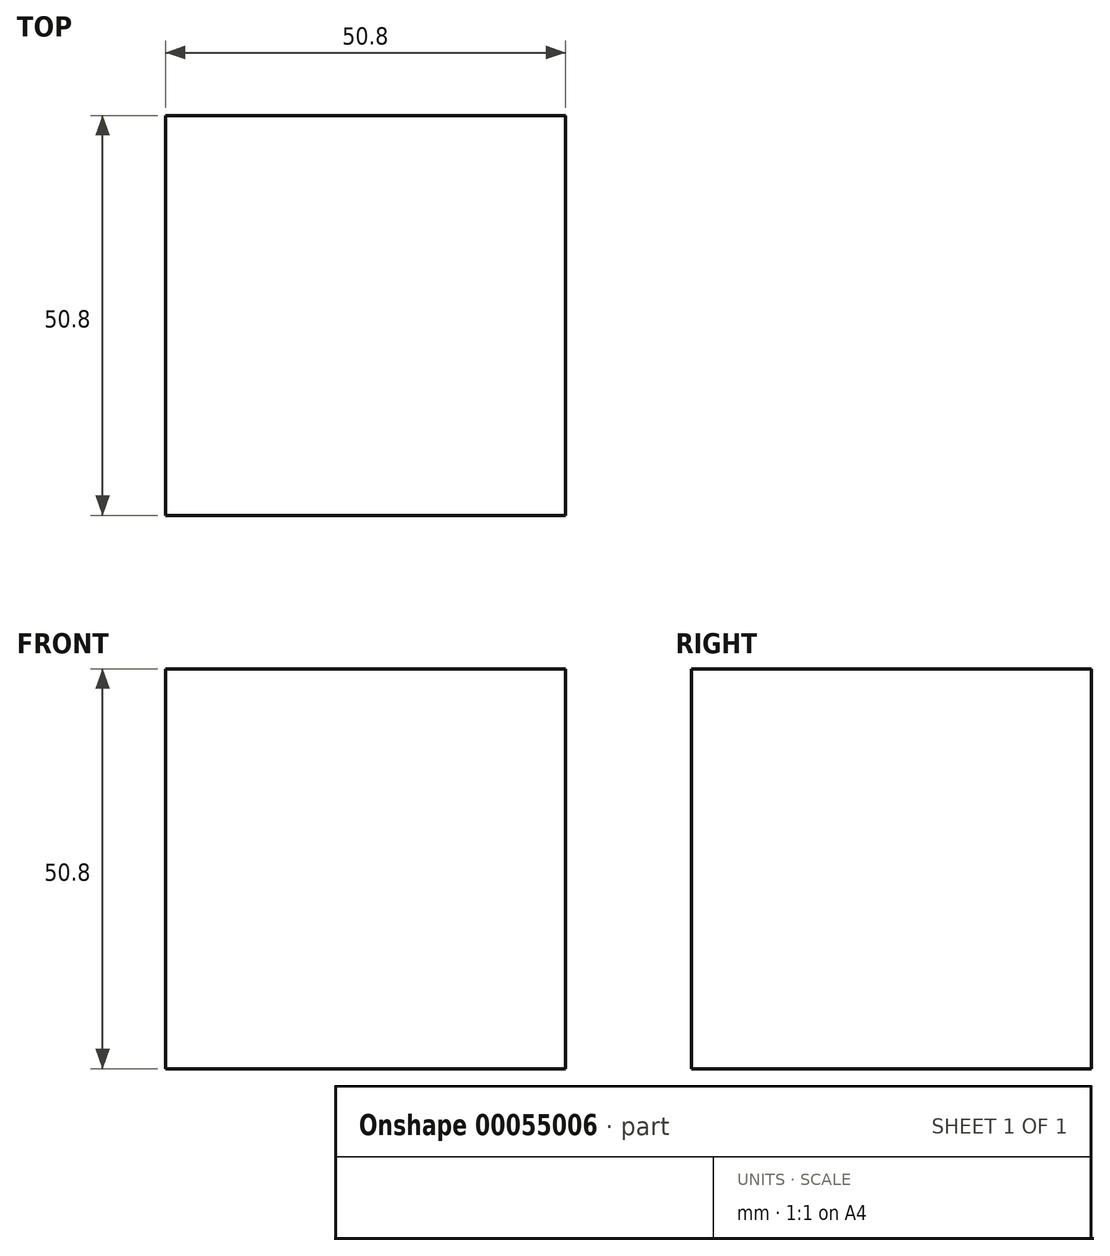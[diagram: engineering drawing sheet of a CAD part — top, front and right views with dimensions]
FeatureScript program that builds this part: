
annotation { "Feature Type Name" : "Feature", "Feature Type Description" : "" }
export const myFeature = defineFeature(function(context is Context, id is Id, definition is map)
    precondition{}
    {
        {
            var Q0;
            Q0=qCreatedBy(makeId("Front.planeOp"),FACE);
            var sketch = newSketch(context, id + "F0", { "sketchPlane" : qUnion([Q0])});
            skLineSegment(sketch, "E0.bottom", {"start": v(0, 0) * mm, "end": v(50.8, 0) * mm});
            skLineSegment(sketch, "E0.top", {"start": v(0, 50.8) * mm, "end": v(50.8, 50.8) * mm});
            skLineSegment(sketch, "E0.left", {"start": v(0, 0) * mm, "end": v(0, 50.8) * mm});
            skLineSegment(sketch, "E0.right", {"start": v(50.8, 0) * mm, "end": v(50.8, 50.8) * mm});
            skSolve(sketch);
        }
        {
            var Q0;
            Q0 = qSketchRegion(id + "F0", true);
            extrude(context, id + "F1", {"entities" : qUnion([Q0]), "depth" : 50.8 * mm});
        }
    });
